# Revit family: QF_ELECTROLUXPROFESSIONAL_1LSN96_WH6-27_S
name_source: partatom
category: Attrezzature speciali
units: mm (PartAtom-declared; Revit-internal decimal feet)

## family parameters
Basato su piano di lavoro = No
Condiviso = No
Punto di calcolo locali = No
Quota connettore circolare = Usa diametro
Sempre verticale = Sì
Taglio con vuoti quando caricato = No
Tipo di parte = Normale

## types (8) — shared parameters
Depth Actual = 990 mm  [stored 3.24803 ft]
Height Actual = 1462 mm  [stored 4.79659 ft]
Latent Heat Output = 0.0
Length Actual = 1020 mm  [stored 3.34646 ft]
Modello = WH6-27
Produttore = Electrolux Professional
Sensible Heat Output = 0.0
URL = www.electroluxprofessional.com
Weight = 425
zero-valued in all types: Gas KW, Prospetto di default, Steam Pounds per Hour

## per-type parameters (varying)
| type | Cycle | Descrizione | Item Number | Phase | Volts | Watts |
| 9868130157 | 50 Hz | WASHER WH6-27 27KG STEAM 200/50/60/3 COMPASS PRO 6H43 JP,EN 2xWATER POWDER+5xLIQ. VALV.OPEN SILVER 2.I/O DISCON. | 1L822H | 3 | 200 V | 2600 W |
| 9868130315 | 50 Hz | WASHER WH6-27 27KG STEAM 220-240/50/1N COMPASS PRO 6H01 ML 2xWATER POWDER+5xLIQ. EL.VALV.OPEN SILVER 2.I/O DISCON. STOP | 1LSPT2 | 1 | 240 V | 2700 W |
| 9868130236 | 60 Hz | WASHER WH6-27 27KG STEAM 220-240/60/1N COMPASS PRO 6G07 ML 2xWATER POWDER+5xLIQ. VALV.OPEN SILVER 2.I/O DISCON. STOP | 1L0GKM | 1 | 240 V | 2600 W |
| 9868130203 | 50 Hz | WASHER WH6-27 27KG STEAM 220-230/50/1N COMPASS PRO 6H12 SE 2xWATER POWDER+5xLIQ. VALV.OPEN SILVER 2.I/O DISCON. STOP | 1L0GDN | 1 | 230 V | 2600 W |
| 9868130189 | 50 Hz | WASHER WH6-27 27KG STEAM 220-240/50/1N COMPASS PRO 6G01 ML 2xWATER POWDER+5xLIQ. VALV.OPEN SILVER 2.I/O DISCON. STOP | 1LA1B8 | 1 | 240 V | 2600 W |
| 9868130249 | 50 Hz | WASHER WH6-27 27KG STEAM 200/50/60/3 COMPASS PRO 6H42 JP,EN 2xWATER POWDER+5xLIQ. VALV.OPEN SILVER 2.I/O QC DISCON. | 1L0GRL | 3 | 200 V | 2600 W |
| 9868130356 | 50 Hz | WASHER WH6-27 27KG STEAM 220-240/50/1N COMPASS PRO 6G01 ML 2xWATER POWDER+5xLIQ. VALV.OPEN SST 2.I/O QC DISCON. STOP | 1L0HE8 | 1 | 240 V | 2700 W |
| 9868130132 | 50 Hz | WASHER WH6-27 27KG STEAM 200/50/60/3 COMPASS PRO 6H43 JP,EN 2xWATER POWDER+5xLIQ. VALV.OPEN SST/SILVER 2.I/O DISCON. | 1LA1CD | 3 | 200 V | 2600 W |

note: [stored X ft] marks values corroborated as IEEE doubles in the binary element streams (Revit-internal decimal feet)

## geometry (parser evidence)
native form markers: Blend x8
no freeform markers — native parametric forms only
